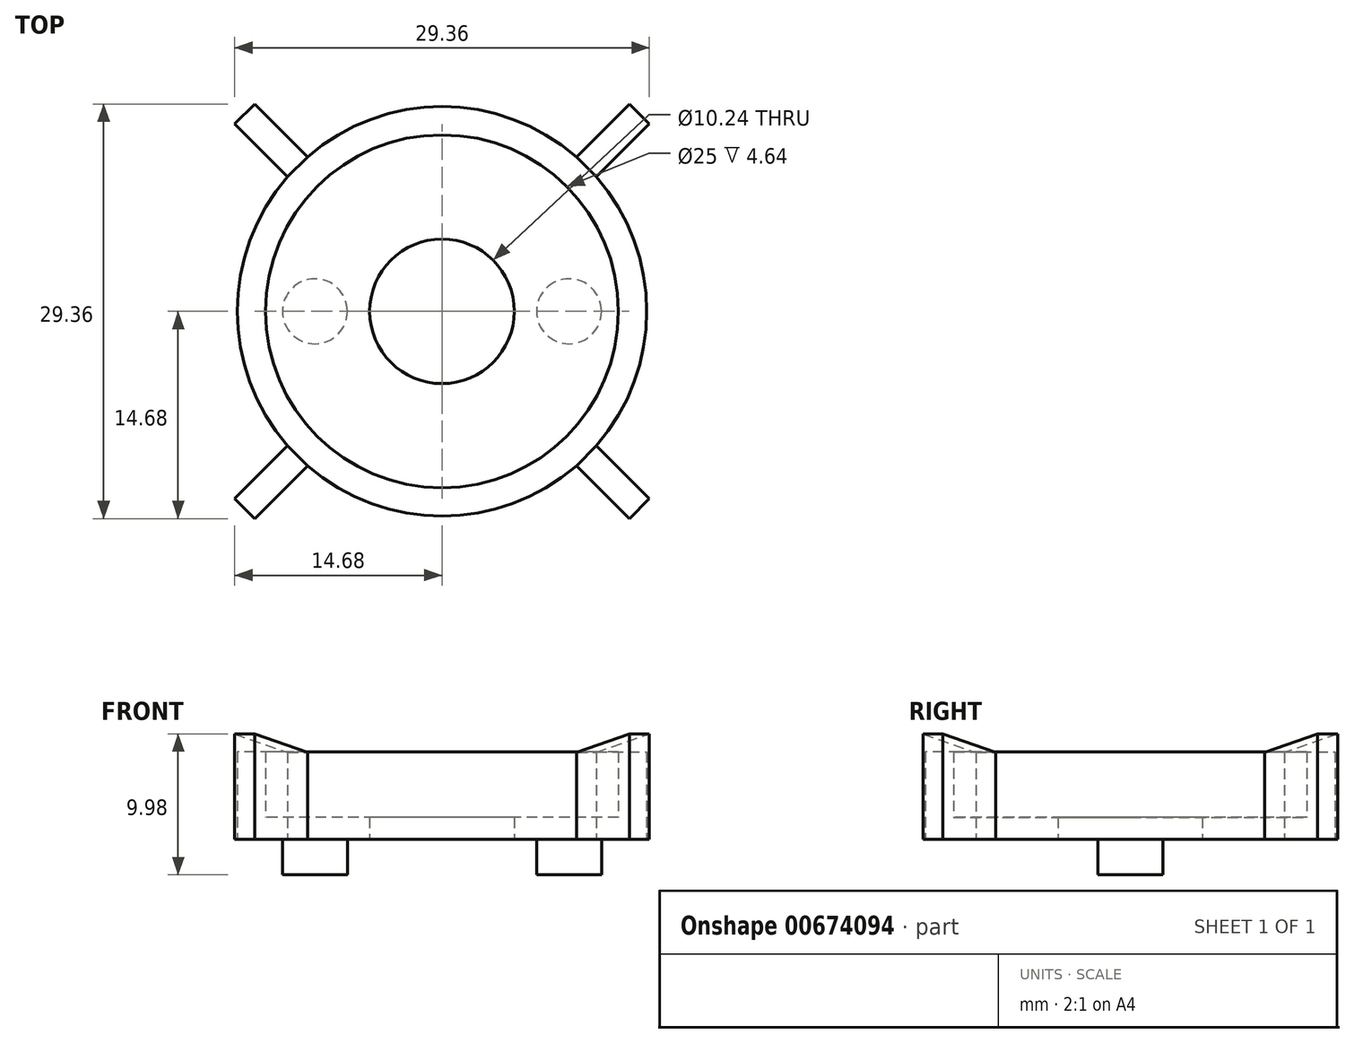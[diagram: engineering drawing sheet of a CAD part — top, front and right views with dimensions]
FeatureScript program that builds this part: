
annotation { "Feature Type Name" : "Feature", "Feature Type Description" : "" }
export const myFeature = defineFeature(function(context is Context, id is Id, definition is map)
    precondition{}
    {
        {
            var Q0;
            Q0=qCreatedBy(makeId("Top.planeOp"),FACE);
            var sketch = newSketch(context, id + "F0", { "sketchPlane" : qUnion([Q0])});
            skCircle(sketch, "E0", {"center": v(0, 0) * mm, "radius": 14.5 * mm});
            skCircle(sketch, "E1", {"center": v(0, 0) * mm, "radius": 5.12 * mm});
            skCircle(sketch, "E2", {"center": v(9, 0) * mm, "radius": 2.3 * mm});
            skCircle(sketch, "E3", {"center": v(-9, 0) * mm, "radius": 2.3 * mm});
            skLineSegment(sketch, "E4", {"start": v(-10.94, 9.52) * mm, "end": v(-14.68, 13.27) * mm});
            skLineSegment(sketch, "E5", {"start": v(-14.68, 13.27) * mm, "end": v(-13.27, 14.68) * mm});
            skLineSegment(sketch, "E6", {"start": v(-13.27, 14.68) * mm, "end": v(-9.52, 10.94) * mm});
            skLineSegment(sketch, "E7", {"start": v(9.52, 10.94) * mm, "end": v(13.27, 14.68) * mm});
            skLineSegment(sketch, "E8", {"start": v(13.27, 14.68) * mm, "end": v(14.68, 13.27) * mm});
            skLineSegment(sketch, "E9", {"start": v(14.68, 13.27) * mm, "end": v(10.94, 9.52) * mm});
            skLineSegment(sketch, "E10", {"start": v(10.94, -9.52) * mm, "end": v(14.68, -13.27) * mm});
            skLineSegment(sketch, "E11", {"start": v(14.68, -13.27) * mm, "end": v(13.27, -14.68) * mm});
            skLineSegment(sketch, "E12", {"start": v(13.27, -14.68) * mm, "end": v(9.52, -10.94) * mm});
            skLineSegment(sketch, "E13", {"start": v(-9.52, -10.94) * mm, "end": v(-13.27, -14.68) * mm});
            skLineSegment(sketch, "E14", {"start": v(-13.27, -14.68) * mm, "end": v(-14.68, -13.27) * mm});
            skLineSegment(sketch, "E15", {"start": v(-14.68, -13.27) * mm, "end": v(-10.94, -9.52) * mm});
            skLineSegment(sketch, "E16", {"start": v(-9, 0) * mm, "end": v(0, 0) * mm});
            skLineSegment(sketch, "E17", {"start": v(0, 0) * mm, "end": v(9, 0) * mm});
            skCircle(sketch, "E18", {"center": v(0, 0) * mm, "radius": 12.5 * mm});
            skSolve(sketch);
        }
        {
            var Q0;
            Q0=makeQuery(id+"F0.imprint","IMPRINT",FACE,{"disambiguationData":[TD([[makeQuery(id+"F0.imprint","IMPRINT",EDGE,{"derivedFrom":sQuery(id+"F0.wireOp",EDGE,"E2")}),-1.0]])]});
            var Q1;
            Q1=makeQuery(id+"F0.imprint","IMPRINT",FACE,{"disambiguationData":[TD([[makeQuery(id+"F0.imprint","IMPRINT",EDGE,{"derivedFrom":sQuery(id+"F0.wireOp",EDGE,"E3")}),1.0]])]});
            var Q2;
            Q2=makeQuery(id+"F0.imprint","IMPRINT",FACE,{"disambiguationData":[TD([[makeQuery(id+"F0.imprint","IMPRINT",EDGE,{"derivedFrom":sQuery(id+"F0.wireOp",EDGE,"E2")}),1.0]])]});
            var Q3;
            Q3=makeQuery(id+"F0.imprint","IMPRINT",FACE,{"disambiguationData":[TD([[makeQuery(id+"F0.imprint","IMPRINT",EDGE,{"derivedFrom":sQuery(id+"F0.wireOp",EDGE,"E18")}),-1.0]])]});
            extrude(context, id + "F1", {"entities" : qUnion([Q0, Q1, Q2, Q3]), "depth" : 1.56 * mm, "offsetDistance" : 25 * mm});
        }
        {
            var Q0;
            Q0=makeQuery(id+"F0.imprint","IMPRINT",FACE,{"disambiguationData":[TD([[makeQuery(id+"F0.imprint","IMPRINT",EDGE,{"derivedFrom":sQuery(id+"F0.wireOp",EDGE,"E18")}),-1.0]])]});
            extrude(context, id + "F2", {"entities" : qUnion([Q0]), "operationType" : NewBodyOperationType.ADD, "depth" : 6.2 * mm, "offsetDistance" : 25 * mm});
        }
        {
            var Q0;
            {var subQ0=sQuery(id+"F0.wireOp",EDGE,"E13");Q0=makeQuery(id+"F0.imprint","IMPRINT",FACE,{"disambiguationData":[TD([[makeQuery(id+"F0.imprint","IMPRINT",EDGE,{"derivedFrom":subQ0}),-1.0]])]});}
            var Q1;
            {var subQ0=sQuery(id+"F0.wireOp",EDGE,"E4");Q1=makeQuery(id+"F0.imprint","IMPRINT",FACE,{"disambiguationData":[TD([[makeQuery(id+"F0.imprint","IMPRINT",EDGE,{"derivedFrom":subQ0}),-1.0]])]});}
            var Q2;
            {var subQ0=sQuery(id+"F0.wireOp",EDGE,"E7");Q2=makeQuery(id+"F0.imprint","IMPRINT",FACE,{"disambiguationData":[TD([[makeQuery(id+"F0.imprint","IMPRINT",EDGE,{"derivedFrom":subQ0}),-1.0]])]});}
            var Q3;
            {var subQ0=sQuery(id+"F0.wireOp",EDGE,"E10");Q3=makeQuery(id+"F0.imprint","IMPRINT",FACE,{"disambiguationData":[TD([[makeQuery(id+"F0.imprint","IMPRINT",EDGE,{"derivedFrom":subQ0}),-1.0]])]});}
            extrude(context, id + "F3", {"entities" : qUnion([Q0, Q1, Q2, Q3]), "operationType" : NewBodyOperationType.ADD, "depth" : (6.8 + .68) * mm, "offsetDistance" : 25 * mm});
        }
        {
            var Q0;
            Q0=makeQuery(id+"F0.imprint","IMPRINT",FACE,{"disambiguationData":[TD([[makeQuery(id+"F0.imprint","IMPRINT",EDGE,{"derivedFrom":sQuery(id+"F0.wireOp",EDGE,"E3")}),1.0]])]});
            var Q1;
            Q1=makeQuery(id+"F0.imprint","IMPRINT",FACE,{"disambiguationData":[TD([[makeQuery(id+"F0.imprint","IMPRINT",EDGE,{"derivedFrom":sQuery(id+"F0.wireOp",EDGE,"E2")}),1.0]])]});
            extrude(context, id + "F4", {"entities" : qUnion([Q0, Q1]), "operationType" : NewBodyOperationType.ADD, "oppositeDirection" : true, "depth" : 2.5 * mm, "offsetDistance" : 25 * mm});
        }
        {
            var Q0;
            Q0=makeQuery(id+"F3.opExtrude","SWEPT_FACE",FACE,{"disambiguationData":[OSD([sQuery(id+"F0.wireOp",EDGE,"E13")])]});
            var sketch = newSketch(context, id + "F5", { "sketchPlane" : qUnion([Q0])});
            skLineSegment(sketch, "E19", {"start": v(-19.77, 7.48) * mm, "end": v(-14.47, 6.17) * mm});
            skLineSegment(sketch, "E20", {"start": v(-14.47, 6.17) * mm, "end": v(-14.47, 7.48) * mm});
            skLineSegment(sketch, "E21", {"start": v(-14.47, 7.48) * mm, "end": v(-19.77, 7.48) * mm});
            skSolve(sketch);
        }
        {
            var Q0;
            {var subQ0=sQuery(id+"F5.wireOp",EDGE,"E19");Q0=makeQuery(id+"F5.imprint","IMPRINT",FACE,{"disambiguationData":[TD([[makeQuery(id+"F5.imprint","IMPRINT",EDGE,{"derivedFrom":subQ0}),1.0]])]});}
            extrude(context, id + "F6", {"entities" : qUnion([Q0]), "oppositeDirection" : true, "depth" : 5 * mm, "offsetDistance" : 25 * mm});
        }
        {
            var Q0;
            Q0=makeQuery(id+"F6.opExtrude","SWEPT_BODY",BODY,{"disambiguationData":[OSD([sQuery(id+"F5.wireOp",EDGE,"E19"),sQuery(id+"F5.wireOp",EDGE,"E20"),sQuery(id+"F5.wireOp",EDGE,"E21")])]});
            var Q1;
            Q1=makeQuery(id+"F2.opExtrude","CAP_EDGE",EDGE,{"disambiguationData":[OSD([sQuery(id+"F0.wireOp",EDGE,"E18")])],"isStart":false});
            circularPattern(context, id + "F7", {"operationType" : NewBodyOperationType.REMOVE, "entities" : qUnion([Q0]), "axis" : qUnion([Q1]), "angle" : 360 * degree, "instanceCount" : 4, "equalSpace" : true});
        }
    });
